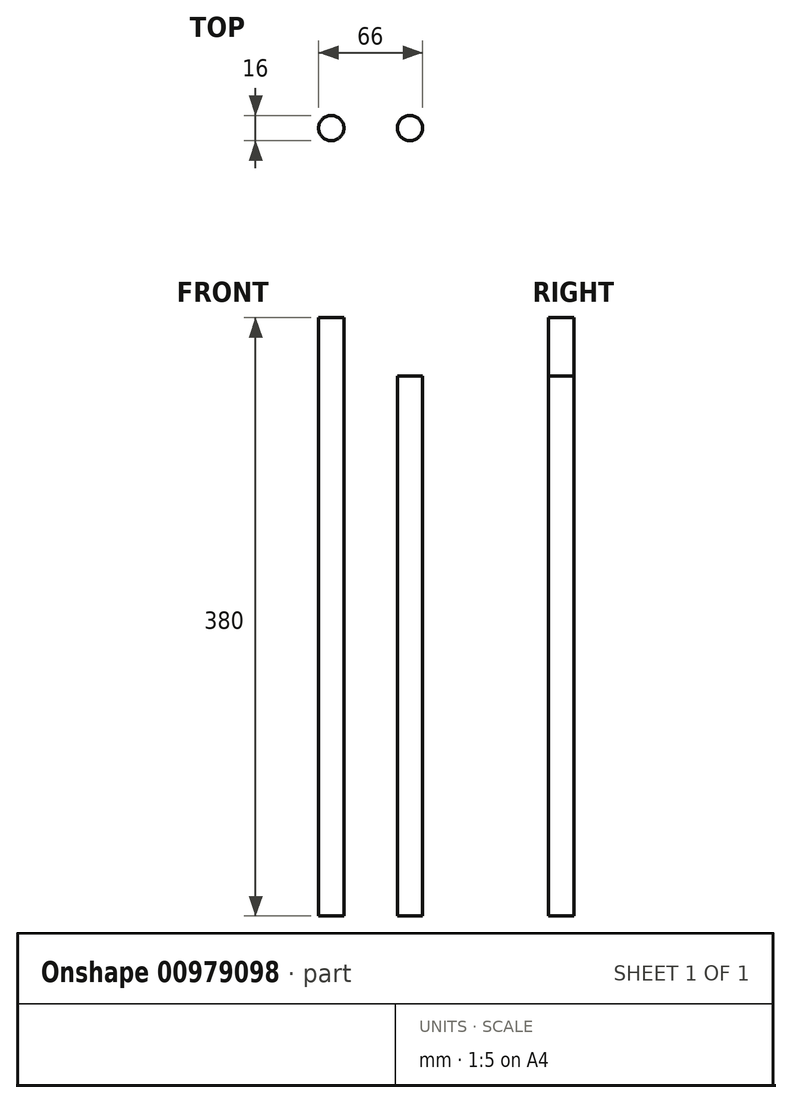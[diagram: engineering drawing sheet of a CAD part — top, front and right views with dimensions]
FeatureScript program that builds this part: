
annotation { "Feature Type Name" : "Feature", "Feature Type Description" : "" }
export const myFeature = defineFeature(function(context is Context, id is Id, definition is map)
    precondition{}
    {
        {
            var Q0;
            Q0=qCreatedBy(makeId("Top.planeOp"),FACE);
            var sketch = newSketch(context, id + "F0", { "sketchPlane" : qUnion([Q0])});
            skCircle(sketch, "E0", {"center": v(-32.55, 7) * mm, "radius": 8 * mm});
            skSolve(sketch);
        }
        {
            var Q0;
            Q0=makeQuery(id+"F0.imprint","IMPRINT",FACE,{"disambiguationData":[TD([[makeQuery(id+"F0.imprint","IMPRINT",EDGE,{"derivedFrom":sQuery(id+"F0.wireOp",EDGE,"E0")}),1.0]])]});
            extrude(context, id + "F1", {"entities" : qUnion([Q0]), "depth" : 380 * mm, "offsetDistance" : 25 * mm});
        }
        {
            var Q0;
            Q0=qSketchRegion(id+"F0",true);
            extrude(context, id + "F2", {"entities" : qUnion([Q0]), "depth" : 343 * mm, "offsetDistance" : 25 * mm});
        }
        {
            var Q0;
            Q0=makeQuery(id+"F2.opExtrude","SWEPT_BODY",BODY,{"disambiguationData":[OSD([sQuery(id+"F0.wireOp",EDGE,"E0")])]});
            transform(context, id + "F3", {"entities" : qUnion([Q0]), "transformType" : TransformType.TRANSLATION_3D, "dx" : 50 * mm, "dy" : 0 * mm, "dz" : 0 * mm, "makeCopy" : false});
        }
    });
